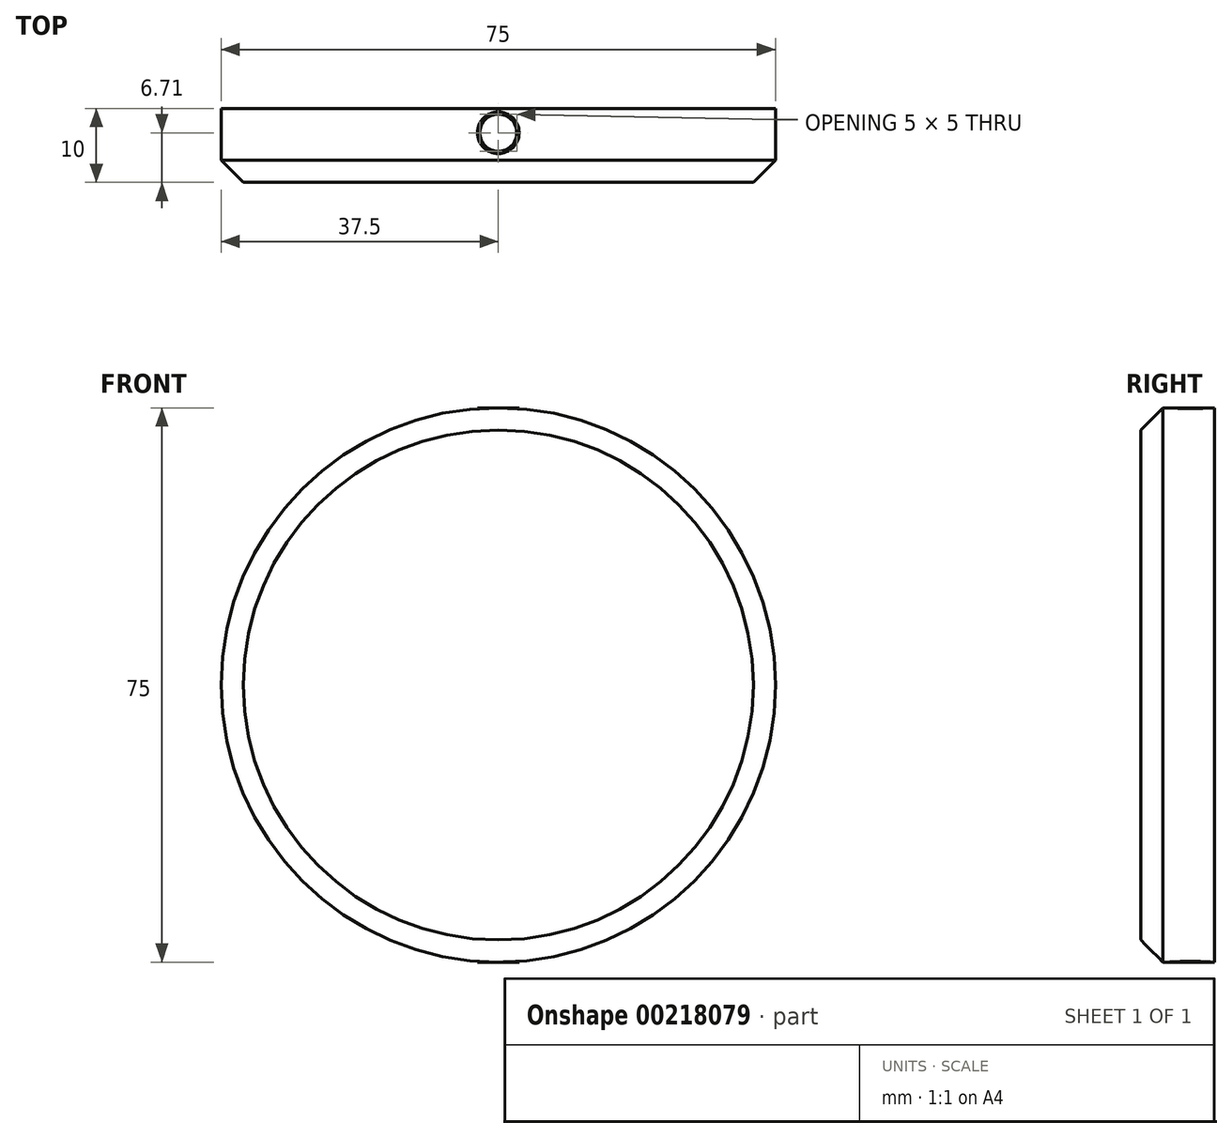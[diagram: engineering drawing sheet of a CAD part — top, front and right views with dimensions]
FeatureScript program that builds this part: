
annotation { "Feature Type Name" : "Feature", "Feature Type Description" : "" }
export const myFeature = defineFeature(function(context is Context, id is Id, definition is map)
    precondition{}
    {
        {
            var Q0;
            Q0=qCreatedBy(makeId("Front.planeOp"),FACE);
            var sketch = newSketch(context, id + "F0", { "sketchPlane" : qUnion([Q0])});
            skPoint(sketch, "E0.orphan", {"position": v(0, -129.07) * mm});
            skLineSegment(sketch, "E1", {"start": v(0, 88.91) * mm, "end": v(0, -176.19) * mm});
            skCircle(sketch, "E2", {"center": v(0, 0) * mm, "radius": 37.5 * mm});
            skSolve(sketch);
        }
        {
            var Q0;
            {var subQ0=sQuery(id+"F0.wireOp",EDGE,"E2");var subQ1=sQuery(id+"F0.wireOp",EDGE,"E1");var subQ2=makeQuery(id+"F0.imprint","INTERSECT",VERTEX,{"disambiguationData":[OD(0.0)],"derivedFrom":[subQ1,subQ0]});Q0=makeQuery(id+"F0.imprint","IMPRINT",FACE,{"disambiguationData":[TD([[makeQuery(id+"F0.imprint","IMPRINT",EDGE,{"disambiguationData":[TD([[subQ2,1.0]])],"derivedFrom":subQ1}),-1.0]])]});}
            var Q1;
            {var subQ0=sQuery(id+"F0.wireOp",EDGE,"E2");var subQ1=sQuery(id+"F0.wireOp",EDGE,"E1");var subQ2=makeQuery(id+"F0.imprint","INTERSECT",VERTEX,{"disambiguationData":[OD(0.0)],"derivedFrom":[subQ1,subQ0]});Q1=makeQuery(id+"F0.imprint","IMPRINT",FACE,{"disambiguationData":[TD([[makeQuery(id+"F0.imprint","IMPRINT",EDGE,{"disambiguationData":[TD([[subQ2,1.0]])],"derivedFrom":subQ1}),1.0]])]});}
            var Q2;
            Q2=sQuery(id+"F0.wireOp",EDGE,"E2");
            extrude(context, id + "F1", {"entities" : qUnion([Q0, Q1]), "surfaceEntities" : qUnion([Q2]), "depth" : 10 * mm});
        }
        {
            var Q0;
            Q0=makeQuery(id+"F1.opExtrude","CAP_EDGE",EDGE,{"disambiguationData":[OSD([sQuery(id+"F0.wireOp",EDGE,"E2")])],"isStart":false});
            chamfer(context, id + "F2", {"entities" : qUnion([Q0]), "width" : 3 * mm});
        }
        {
            var Q0;
            Q0=qCreatedBy(makeId("Top.planeOp"),FACE);
            var sketch = newSketch(context, id + "F3", { "sketchPlane" : qUnion([Q0])});
            skCircle(sketch, "E3", {"center": v(0, -3.3) * mm, "radius": 2.5 * mm});
            skCircle(sketch, "E4", {"center": v(0, -3.3) * mm, "radius": 2.82 * mm});
            skSolve(sketch);
        }
        {
            var Q0;
            Q0 = qSketchRegion(id + "F3", true);
            extrude(context, id + "F4", {"entities" : qUnion([Q0]), "operationType" : NewBodyOperationType.ADD, "endBound" : BoundingType.SYMMETRIC, "depth" : 75 * mm});
        }
        {
            var Q0;
            Q0=makeQuery(id+"F4.opExtrude","CAP_FACE",FACE,{"disambiguationData":[OSD([sQuery(id+"F3.wireOp",EDGE,"E3"),sQuery(id+"F3.wireOp",EDGE,"E4")])],"isStart":true});
            extrude(context, id + "F5", {"entities" : qUnion([Q0]), "operationType" : NewBodyOperationType.ADD, "oppositeDirection" : true, "depth" : 75 * mm});
        }
    });
